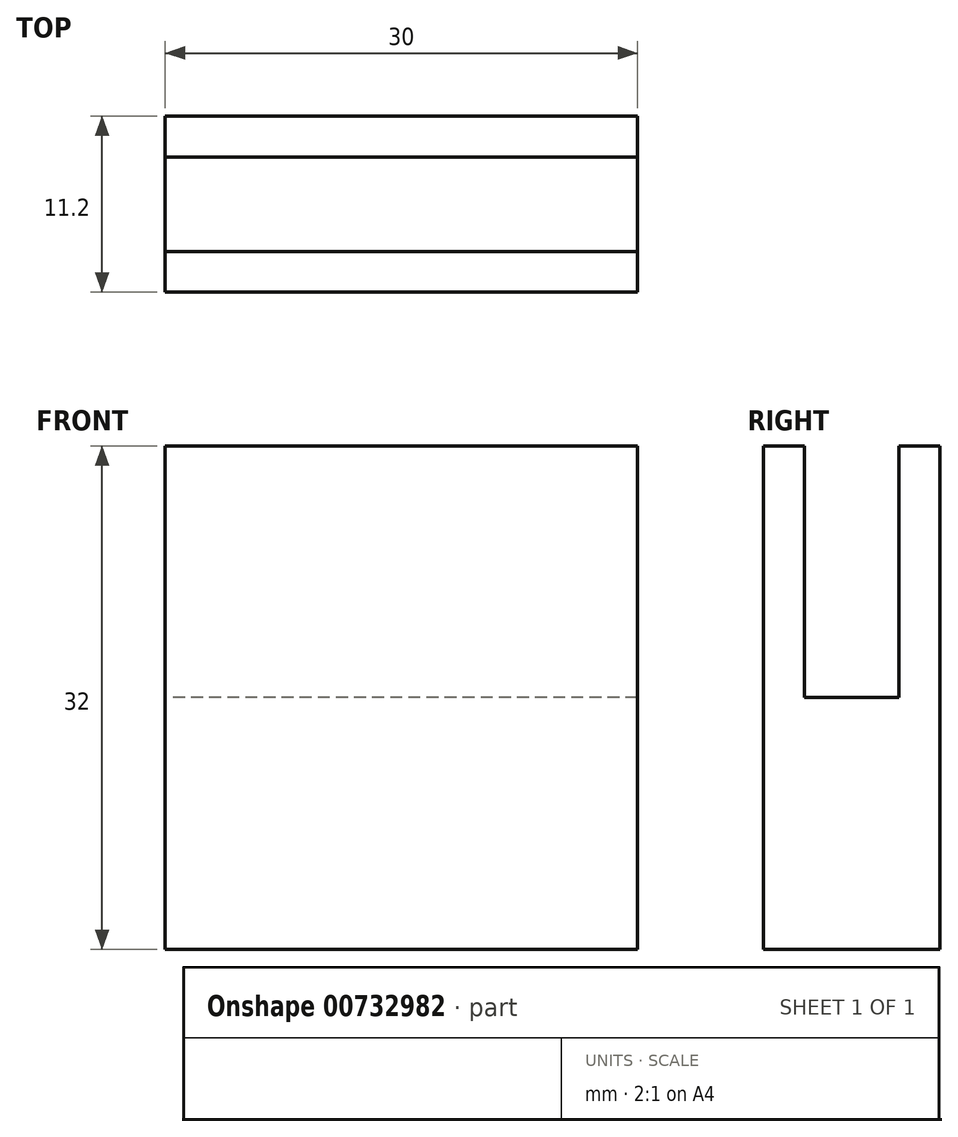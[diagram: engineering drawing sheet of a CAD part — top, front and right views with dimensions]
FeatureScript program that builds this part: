
annotation { "Feature Type Name" : "Feature", "Feature Type Description" : "" }
export const myFeature = defineFeature(function(context is Context, id is Id, definition is map)
    precondition{}
    {
        {
            var Q0;
            Q0=qCreatedBy(makeId("Top.planeOp"),FACE);
            var sketch = newSketch(context, id + "F0", { "sketchPlane" : qUnion([Q0])});
            skLineSegment(sketch, "E0.bottom", {"start": v(0, 0) * mm, "end": v(-30, 0) * mm});
            skLineSegment(sketch, "E0.top", {"start": v(0, -11.2) * mm, "end": v(-30, -11.2) * mm});
            skLineSegment(sketch, "E0.left", {"start": v(0, 0) * mm, "end": v(0, -11.2) * mm});
            skLineSegment(sketch, "E0.right", {"start": v(-30, 0) * mm, "end": v(-30, -11.2) * mm});
            skSolve(sketch);
        }
        {
            var Q0;
            Q0=makeQuery(id+"F0.imprint","IMPRINT",FACE,{"disambiguationData":[TD([[makeQuery(id+"F0.imprint","IMPRINT",EDGE,{"derivedFrom":sQuery(id+"F0.wireOp",EDGE,"E0.bottom")}),1.0]])]});
            extrude(context, id + "F1", {"entities" : qUnion([Q0]), "depth" : 32 * mm, "offsetDistance" : 25 * mm});
        }
        {
            var Q0;
            Q0=makeQuery(id+"F1.opExtrude","CAP_FACE",FACE,{"disambiguationData":[OSD([sQuery(id+"F0.wireOp",EDGE,"E0.bottom"),sQuery(id+"F0.wireOp",EDGE,"E0.top"),sQuery(id+"F0.wireOp",EDGE,"E0.left"),sQuery(id+"F0.wireOp",EDGE,"E0.right")])],"isStart":false});
            var sketch = newSketch(context, id + "F2", { "sketchPlane" : qUnion([Q0])});
            skLineSegment(sketch, "E1.bottom", {"start": v(0, -2.6) * mm, "end": v(-30, -2.6) * mm});
            skLineSegment(sketch, "E1.top", {"start": v(0, -8.6) * mm, "end": v(-30, -8.6) * mm});
            skLineSegment(sketch, "E1.left", {"start": v(0, -2.6) * mm, "end": v(0, -8.6) * mm});
            skLineSegment(sketch, "E1.right", {"start": v(-30, -2.6) * mm, "end": v(-30, -8.6) * mm});
            skPoint(sketch, "E1.middle", {"position": v(-15, -5.6) * mm});
            skPoint(sketch, "E1.middle.positionSnap0", {"position": v(-15, -11.2) * mm});
            skPoint(sketch, "E1.centerSnap0", {"position": v(-15, -11.2) * mm});
            skSolve(sketch);
        }
        {
            var Q0;
            Q0=makeQuery(id+"F2.imprint","IMPRINT",FACE,{"disambiguationData":[TD([[makeQuery(id+"F2.imprint","IMPRINT",EDGE,{"derivedFrom":sQuery(id+"F2.wireOp",EDGE,"E1.bottom")}),1.0]])]});
            extrude(context, id + "F3", {"entities" : qUnion([Q0]), "operationType" : NewBodyOperationType.REMOVE, "oppositeDirection" : true, "depth" : 16 * mm, "offsetDistance" : 25 * mm});
        }
    });
